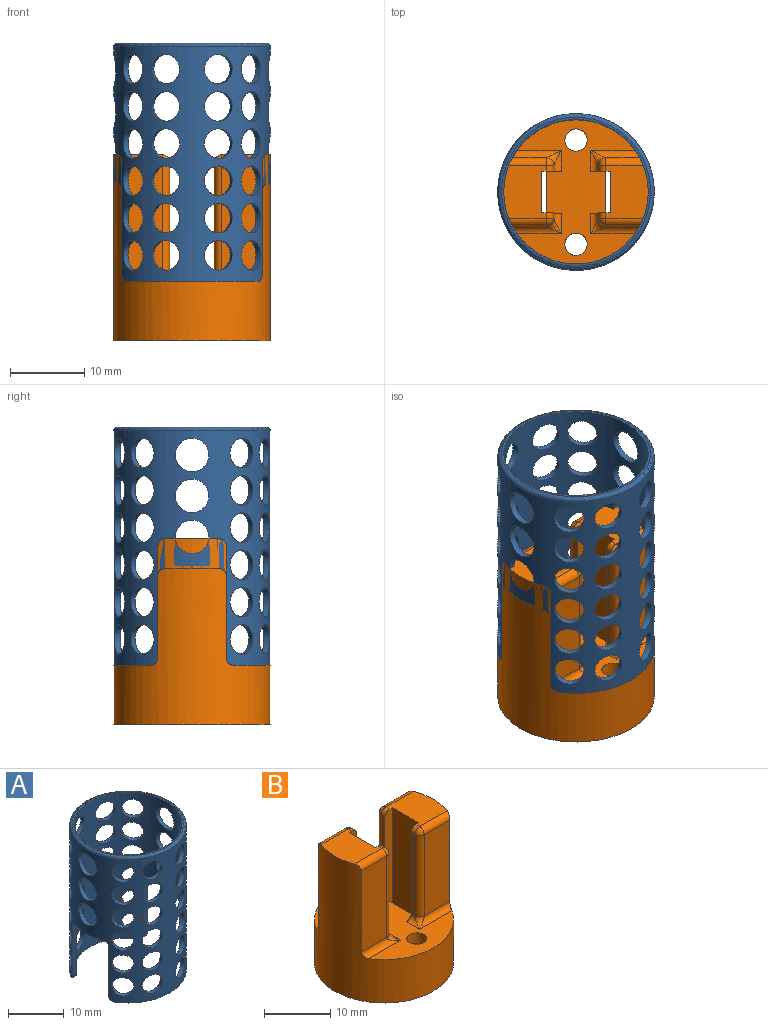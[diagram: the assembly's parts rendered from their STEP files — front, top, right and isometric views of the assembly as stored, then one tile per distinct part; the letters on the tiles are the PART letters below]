
ASSEMBLY  parts=2 mates=1
PART A: 74 faces, bbox 22.8x22.8x32 mm
  f0: cylinder r=9.7mm len=32mm, axis (0,0,-1), area 999.1mm2, adj f2,f3,f4,f5,f6,f7,f8,f9
  f1: cylinder r=10.5mm len=31.5mm, axis (0,0,-1), area 1129.1mm2, adj f2,f4,f5,f6,f7,f8,f9,f10
  f2: plane 17.76x4.9mm, normal (0,0,-1), area 15.9mm2, adj f0,f1,f61,f63
  f3: plane 20x20mm, normal (0,0,1), area 18.6mm2, adj f0,f73
  f4: plane 17.76x4.9mm, normal (0,0,-1), area 15.9mm2, adj f0,f1,f62,f66
  f5: plane 11.02x0.92mm, normal (0,1,0), area 9.8mm2, adj f0,f1,f17,f18,f65,f66
  f6: plane 7.2x1.49mm, normal (0,0,-1), area 5.9mm2, adj f0,f1,f64,f65
  f7: plane 11.02x0.92mm, normal (0,-1,0), area 9.8mm2, adj f0,f1,f15,f16,f63,f64
  f8: plane 7.2x1.49mm, normal (0,0,-1), area 5.9mm2, adj f0,f1,f59,f60
  f9: plane 11.02x0.92mm, normal (0,-1,0), area 9.8mm2, adj f0,f1,f13,f14,f59,f61
  f10: plane 11.02x0.92mm, normal (0,1,0), area 9.8mm2, adj f0,f1,f11,f12,f60,f62
  f11: cylinder r=2mm len=4mm, axis (-0.77,0.64,0), area 10.1mm2, adj f0,f1,f10
  f12: cylinder r=2mm len=4mm, axis (-0.77,0.64,0), area 10.1mm2, adj f0,f1,f10
  f13: cylinder r=2mm len=4mm, axis (-0.77,-0.64,0), area 10.1mm2, adj f0,f1,f9
  f14: cylinder r=2mm len=4mm, axis (-0.77,-0.64,0), area 10.1mm2, adj f0,f1,f9
  f15: cylinder r=2mm len=4mm, axis (0.77,-0.64,0), area 10.1mm2, adj f0,f1,f7
  f16: cylinder r=2mm len=4mm, axis (0.77,-0.64,0), area 10.1mm2, adj f0,f1,f7
  f17: cylinder r=2mm len=4mm, axis (0.77,0.64,0), area 10.1mm2, adj f0,f1,f5
  f18: cylinder r=2mm len=4mm, axis (0.77,0.64,0), area 10.1mm2, adj f0,f1,f5
  f19: cylinder r=2mm len=4.1mm, axis (-0.34,-0.94,0), area 10.2mm2, adj f0,f1
  f20: cylinder r=2mm len=4mm, axis (-0.77,-0.64,0), area 10.2mm2, adj f0,f1
  f21: cylinder r=2mm len=4.1mm, axis (0.34,-0.94,0), area 10.2mm2, adj f0,f1
  f22: cylinder r=2mm len=4mm, axis (0.77,-0.64,0), area 10.2mm2, adj f0,f1
  f23: cylinder r=2mm len=4.1mm, axis (-0.34,0.94,0), area 10.2mm2, adj f0,f1
  f24: cylinder r=2mm len=4mm, axis (-0.77,0.64,0), area 10.2mm2, adj f0,f1
  f25: cylinder r=2mm len=4.1mm, axis (0.34,0.94,0), area 10.2mm2, adj f0,f1
  f26: cylinder r=2mm len=4mm, axis (0.77,0.64,0), area 10.2mm2, adj f0,f1
  f27: cylinder r=2mm len=4.1mm, axis (-0.34,-0.94,0), area 10.2mm2, adj f0,f1
  f28: cylinder r=2mm len=4mm, axis (-0.77,-0.64,0), area 10.2mm2, adj f0,f1
  f29: cylinder r=2mm len=4.1mm, axis (0.34,-0.94,0), area 10.2mm2, adj f0,f1
  f30: cylinder r=2mm len=4mm, axis (0.77,-0.64,0), area 10.2mm2, adj f0,f1
  f31: cylinder r=2mm len=4.1mm, axis (-0.34,0.94,0), area 10.2mm2, adj f0,f1
  f32: cylinder r=2mm len=4mm, axis (-0.77,0.64,0), area 10.2mm2, adj f0,f1
  f33: cylinder r=2mm len=4.1mm, axis (0.34,0.94,0), area 10.2mm2, adj f0,f1
  f34: cylinder r=2mm len=4mm, axis (0.77,0.64,0), area 10.2mm2, adj f0,f1
  f35: cylinder r=2mm len=4.1mm, axis (-0.34,-0.94,0), area 10.2mm2, adj f0,f1
  f36: cylinder r=2mm len=4mm, axis (-0.77,-0.64,0), area 10.2mm2, adj f0,f1
  f37: cylinder r=2mm len=4.1mm, axis (0.34,-0.94,0), area 10.2mm2, adj f0,f1
  f38: cylinder r=2mm len=4mm, axis (0.77,-0.64,0), area 10.2mm2, adj f0,f1
  f39: cylinder r=2mm len=4.1mm, axis (-0.34,0.94,0), area 10.2mm2, adj f0,f1
  f40: cylinder r=2mm len=4mm, axis (-0.77,0.64,0), area 10.2mm2, adj f0,f1
  f41: cylinder r=2mm len=4.1mm, axis (0.34,0.94,0), area 10.2mm2, adj f0,f1
  f42: cylinder r=2mm len=4mm, axis (0.77,0.64,0), area 10.2mm2, adj f0,f1
  f43: cylinder r=2mm len=4.1mm, axis (-0.34,-0.94,0), area 10.2mm2, adj f0,f1
  f44: cylinder r=2mm len=4mm, axis (-0.77,-0.64,0), area 10.2mm2, adj f0,f1
  f45: cylinder r=2mm len=4.1mm, axis (0.34,-0.94,0), area 10.2mm2, adj f0,f1
  f46: cylinder r=2mm len=4mm, axis (0.77,-0.64,0), area 10.2mm2, adj f0,f1
  f47: cylinder r=2mm len=4.1mm, axis (-0.34,0.94,0), area 10.2mm2, adj f0,f1
  f48: cylinder r=2mm len=4mm, axis (-0.77,0.64,0), area 10.2mm2, adj f0,f1
  f49: cylinder r=2mm len=4.1mm, axis (0.34,0.94,0), area 10.2mm2, adj f0,f1
  f50: cylinder r=2mm len=4mm, axis (0.77,0.64,0), area 10.2mm2, adj f0,f1
  f51: cylinder r=2mm len=4.1mm, axis (-0.34,-0.94,0), area 10.2mm2, adj f0,f1
  f52: cylinder r=2mm len=4.1mm, axis (0.34,-0.94,0), area 10.2mm2, adj f0,f1
  f53: cylinder r=2mm len=4.1mm, axis (-0.34,0.94,0), area 10.2mm2, adj f0,f1
  f54: cylinder r=2mm len=4.1mm, axis (0.34,0.94,0), area 10.2mm2, adj f0,f1
  f55: cylinder r=2mm len=4.1mm, axis (-0.34,-0.94,0), area 10.2mm2, adj f0,f1
  f56: cylinder r=2mm len=4.1mm, axis (0.34,-0.94,0), area 10.2mm2, adj f0,f1
  f57: cylinder r=2mm len=4.1mm, axis (-0.34,0.94,0), area 10.2mm2, adj f0,f1
  f58: cylinder r=2mm len=4.1mm, axis (0.34,0.94,0), area 10.2mm2, adj f0,f1
  f59: cylinder r=1mm len=1.32mm, axis (-1,0,0), area 1.4mm2, adj f0,f1,f8,f9
  f60: cylinder r=1mm len=1.32mm, axis (-1,0,0), area 1.4mm2, adj f0,f1,f8,f10
  f61: cylinder r=1mm len=1.52mm, axis (-1,0,0), area 1.4mm2, adj f0,f1,f2,f9
  f62: cylinder r=1mm len=1.52mm, axis (-1,0,0), area 1.4mm2, adj f0,f1,f4,f10
  f63: cylinder r=1mm len=1.52mm, axis (-1,0,0), area 1.4mm2, adj f0,f1,f2,f7
  f64: cylinder r=1mm len=1.32mm, axis (-1,0,0), area 1.4mm2, adj f0,f1,f6,f7
  f65: cylinder r=1mm len=1.32mm, axis (-1,0,0), area 1.4mm2, adj f0,f1,f5,f6
  f66: cylinder r=1mm len=1.52mm, axis (-1,0,0), area 1.4mm2, adj f0,f1,f4,f5
  f67: cylinder r=2.25mm len=4.5mm, axis (1,0,0), area 11.5mm2, adj f0,f1
  f68: cylinder r=2.25mm len=4.5mm, axis (1,0,0), area 11.5mm2, adj f0,f1
  f69: cylinder r=2.25mm len=4.5mm, axis (1,0,0), area 11.5mm2, adj f0,f1
  f70: cylinder r=2.25mm len=4.5mm, axis (1,0,0), area 11.5mm2, adj f0,f1
  f71: cylinder r=2.25mm len=4.5mm, axis (1,0,0), area 11.5mm2, adj f0,f1
  f72: cylinder r=2.25mm len=4.5mm, axis (1,0,0), area 11.5mm2, adj f0,f1
  f73: torus R=10mm, axis (0,0,1), area 50.9mm2, adj f1,f3
PART B: 116 faces, bbox 21.3x21.3x25.3 mm
  f0: plane 7.2x6.5mm, normal (0,0,1), area 41.9mm2, adj f2,f40,f41,f44,f56,f57,f58,f59
  f1: plane 12.4x9.4mm, normal (0,0,-1), area 26.6mm2, adj f21,f23,f24,f27,f29,f30,f48,f50
  f2: cylinder r=10.5mm len=25mm, axis (0,0,1), area 851.6mm2, adj f0,f3,f6,f31,f32,f37,f38,f43
  f3: plane 7.2x6.5mm, normal (0,0,1), area 41.9mm2, adj f2,f34,f35,f46,f60,f61,f62,f63
  f4: cylinder r=1.5mm len=3.34mm, axis (0,0,-1), area 23.1mm2, adj f18,f31,f100
  f5: cylinder r=1.5mm len=3.34mm, axis (0,0,-1), area 23.1mm2, adj f12,f31,f101
  f6: plane 21x21mm, normal (0,0,-1), area 119.9mm2, adj f2,f7,f8,f9,f10,f11,f13,f14
  f7: plane 4.5x1.2mm, normal (-1,0,0), area 5.4mm2, adj f6,f8,f98,f105
  f8: plane 4.5x4.13mm, normal (0,1,0), area 18.6mm2, adj f6,f7,f99,f104
  f9: plane 4.5x1.55mm, normal (0.91,0.41,0), area 7.6mm2, adj f6,f10,f99,f102
  f10: plane 6.26x5.16mm, normal (0,1,0), area 18.8mm2, adj f6,f9,f11,f101,f102
  f11: cylinder r=9mm len=11.01mm, axis (0,0,-1), area 37.1mm2, adj f6,f10,f101,f108
  f12: plane 3.92x1.71mm, normal (0,0,-1), area 4.8mm2, adj f5,f101,f102,f103,f104,f106
  f13: cylinder r=9mm len=11.01mm, axis (0,0,-1), area 37.1mm2, adj f6,f17,f100,f115
  f14: plane 4.5x1.2mm, normal (1,0,0), area 5.4mm2, adj f6,f15,f95,f112
  f15: plane 4.5x4.13mm, normal (0,-1,0), area 18.6mm2, adj f6,f14,f94,f111
  f16: plane 4.5x1.55mm, normal (-0.91,-0.41,0), area 7.6mm2, adj f6,f17,f94,f109
  f17: plane 6.26x5.16mm, normal (0,-1,0), area 18.8mm2, adj f6,f13,f16,f100,f109
  f18: plane 3.92x1.71mm, normal (0,0,-1), area 4.8mm2, adj f4,f100,f109,f110,f111,f113
  f19: cylinder r=9.7mm len=8.05mm, axis (0,0,-1), area 20.8mm2, adj f6,f30,f85,f89
  f20: plane 4.4x2.16mm, normal (0,1,0), area 8.7mm2, adj f6,f86,f87,f88,f89
  f21: plane 6.33x3.65mm, normal (0.91,0.41,0), area 12.1mm2, adj f1,f6,f22,f49,f51,f86,f87,f97
  f22: plane 6.4x4.4mm, normal (0,1,0), area 28.2mm2, adj f6,f21,f23,f97
  f23: plane 6x4.6mm, normal (-1,0,0), area 18.5mm2, adj f1,f6,f22,f24,f97
  f24: plane 6x5.29mm, normal (0,1,0), area 28.6mm2, adj f1,f6,f23,f25,f84
  f25: cylinder r=9.7mm len=8.05mm, axis (0,0,-1), area 20.8mm2, adj f6,f24,f84,f93
  f26: plane 4.4x2.16mm, normal (0,-1,0), area 8.7mm2, adj f6,f90,f91,f92,f93
  f27: plane 6.33x3.65mm, normal (-0.91,-0.41,0), area 12.1mm2, adj f1,f6,f28,f53,f55,f90,f91,f96
  f28: plane 6.4x4.4mm, normal (0,-1,0), area 28.2mm2, adj f6,f27,f29,f96
  f29: plane 6x4.6mm, normal (1,0,0), area 18.5mm2, adj f1,f6,f28,f30,f96
  f30: plane 6x5.29mm, normal (0,-1,0), area 28.6mm2, adj f1,f6,f19,f29,f85
  f31: plane 21x17.76mm, normal (0,0,1), area 175.9mm2, adj f2,f4,f5,f34,f35,f40,f41,f45
  f32: plane 15x5.44mm, normal (0,-1,0), area 81.6mm2, adj f2,f62,f70,f73
  f33: plane 15x0.8mm, normal (-1,0,0), area 12mm2, adj f34,f63,f71,f73
  f34: plane 18.75x2.6mm, normal (0,1,0), area 28.2mm2, adj f3,f31,f33,f46,f47,f49,f63,f71
  f35: plane 18.75x2.6mm, normal (0,-1,0), area 28.2mm2, adj f3,f31,f36,f46,f47,f50,f60,f68
  f36: plane 15x0.8mm, normal (-1,0,0), area 12mm2, adj f35,f60,f68,f76
  f37: plane 15x5.44mm, normal (0,1,0), area 81.6mm2, adj f2,f61,f69,f76
  f38: plane 15x5.44mm, normal (0,1,0), area 81.6mm2, adj f2,f58,f66,f79
  f39: plane 15x0.8mm, normal (1,0,0), area 12mm2, adj f40,f59,f67,f79
  f40: plane 18.75x2.6mm, normal (0,-1,0), area 28.2mm2, adj f0,f31,f39,f44,f45,f53,f59,f67
  f41: plane 18.75x2.6mm, normal (0,1,0), area 28.2mm2, adj f0,f31,f42,f44,f45,f54,f56,f64
  f42: plane 15x0.8mm, normal (1,0,0), area 12mm2, adj f41,f56,f64,f82
  f43: plane 15x5.44mm, normal (0,-1,0), area 81.6mm2, adj f2,f57,f65,f82
  f44: plane 18.75x5.6mm, normal (1,0,0), area 105mm2, adj f0,f40,f41,f52
  f45: plane 5.6x1.75mm, normal (-1,0,0), area 9.8mm2, adj f31,f40,f41,f55
  f46: plane 18.75x5.6mm, normal (-1,0,0), area 105mm2, adj f3,f34,f35,f48
  f47: plane 5.6x1.75mm, normal (1,0,0), area 9.8mm2, adj f31,f34,f35,f51
  f48: plane 6.14x0.29mm, normal (-0.71,0,-0.71), area 2.1mm2, adj f1,f46,f49,f50,f87
  f49: plane 1.09x0.27mm, normal (0,0.71,-0.71), area 0.3mm2, adj f21,f34,f48,f51,f87
  f50: plane 1.1x0.25mm, normal (0,-0.71,-0.71), area 0.3mm2, adj f1,f35,f48,f51
  f51: plane 6.07x0.25mm, normal (0.71,0,-0.71), area 2.1mm2, adj f1,f21,f47,f49,f50
  f52: plane 6.14x0.29mm, normal (0.71,0,-0.71), area 2.1mm2, adj f1,f44,f53,f54,f91
  f53: plane 1.09x0.27mm, normal (0,-0.71,-0.71), area 0.3mm2, adj f27,f40,f52,f55,f91
  f54: plane 1.1x0.25mm, normal (0,0.71,-0.71), area 0.3mm2, adj f1,f41,f52,f55
  f55: plane 6.07x0.25mm, normal (-0.71,0,-0.71), area 2.1mm2, adj f1,f27,f45,f53,f54
  f56: cylinder r=1mm len=1mm, axis (0,1,0), area 1.3mm2, adj f0,f41,f42,f81
  f57: cylinder r=1mm len=5.86mm, axis (1,0,0), area 8.9mm2, adj f0,f2,f43,f81
  f58: cylinder r=1mm len=5.86mm, axis (-1,0,0), area 8.9mm2, adj f0,f2,f38,f78
  f59: cylinder r=1mm len=1mm, axis (0,1,0), area 1.3mm2, adj f0,f39,f40,f78
  f60: cylinder r=1mm len=1mm, axis (0,-1,0), area 1.3mm2, adj f3,f35,f36,f75
  f61: cylinder r=1mm len=5.86mm, axis (-1,0,0), area 8.9mm2, adj f2,f3,f37,f75
  f62: cylinder r=1mm len=5.86mm, axis (1,0,0), area 8.9mm2, adj f2,f3,f32,f72
  f63: cylinder r=1mm len=1mm, axis (0,-1,0), area 1.3mm2, adj f3,f33,f34,f72
  f64: cylinder r=1mm len=2.8mm, axis (0,-1,0), area 2.4mm2, adj f31,f41,f42,f83
  f65: cylinder r=1mm len=7.44mm, axis (-1,0,0), area 9.2mm2, adj f2,f31,f43,f83
  f66: cylinder r=1mm len=7.44mm, axis (1,0,0), area 9.2mm2, adj f2,f31,f38,f80
  f67: cylinder r=1mm len=2.8mm, axis (0,-1,0), area 2.4mm2, adj f31,f39,f40,f80
  f68: cylinder r=1mm len=2.8mm, axis (0,1,0), area 2.4mm2, adj f31,f35,f36,f77
  f69: cylinder r=1mm len=7.44mm, axis (1,0,0), area 9.2mm2, adj f2,f31,f37,f77
  f70: cylinder r=1mm len=7.44mm, axis (-1,0,0), area 9.2mm2, adj f2,f31,f32,f74
  f71: cylinder r=1mm len=2.8mm, axis (0,1,0), area 2.4mm2, adj f31,f33,f34,f74
  f72: sphere r=1mm, area 1.6mm2, adj f62,f63,f73
  f73: cylinder r=1mm len=15mm, axis (0,0,1), area 23.6mm2, adj f32,f33,f72,f74
  f74: bspline ~2x2mm, area 1.9mm2, adj f70,f71,f73
  f75: sphere r=1mm, area 1.6mm2, adj f60,f61,f76
  f76: cylinder r=1mm len=15mm, axis (0,0,1), area 23.6mm2, adj f36,f37,f75,f77
  f77: bspline ~2x2mm, area 1.9mm2, adj f68,f69,f76
  f78: sphere r=1mm, area 1.6mm2, adj f58,f59,f79
  f79: cylinder r=1mm len=15mm, axis (0,0,1), area 23.6mm2, adj f38,f39,f78,f80
  f80: bspline ~2x2mm, area 1.9mm2, adj f66,f67,f79
  f81: sphere r=1mm, area 1.6mm2, adj f56,f57,f82
  f82: cylinder r=1mm len=15mm, axis (0,0,1), area 23.6mm2, adj f42,f43,f81,f83
  f83: bspline ~2x2mm, area 1.9mm2, adj f64,f65,f82
  f84: torus R=6.2mm, axis (0,0,-1), area 45.4mm2, adj f1,f24,f25,f92
  f85: torus R=6.2mm, axis (0,0,-1), area 45.4mm2, adj f1,f19,f30,f88
  f86: cylinder r=1.6mm len=5.86mm, axis (0,0,1), area 9.5mm2, adj f6,f20,f21,f87
  f87: cylinder r=1.6mm len=1.72mm, axis (1,0,0), area 2.5mm2, adj f1,f20,f21,f48,f49,f86,f88
  f88: bspline ~4.19x3.94mm, area 9.8mm2, adj f20,f85,f87,f89
  f89: cylinder r=1.6mm len=2.5mm, axis (0,0,-1), area 4.9mm2, adj f6,f19,f20,f88
  f90: cylinder r=1.6mm len=5.86mm, axis (0,0,1), area 9.5mm2, adj f6,f26,f27,f91
  f91: cylinder r=1.6mm len=1.72mm, axis (-1,0,0), area 2.5mm2, adj f1,f26,f27,f52,f53,f90,f92
  f92: bspline ~4.19x3.94mm, area 9.8mm2, adj f26,f84,f91,f93
  f93: cylinder r=1.6mm len=2.5mm, axis (0,0,-1), area 4.9mm2, adj f6,f25,f26,f92
  f94: cylinder r=1.6mm len=4.5mm, axis (0,0,1), area 8.3mm2, adj f6,f15,f16,f110
  f95: cylinder r=1.6mm len=4.5mm, axis (0,0,-1), area 8.7mm2, adj f6,f14,f113,f114,f115
  f96: cylinder r=1.6mm len=6.4mm, axis (1,0,0), area 15.2mm2, adj f1,f27,f28,f29
  f97: cylinder r=1.6mm len=6.4mm, axis (-1,0,0), area 15.2mm2, adj f1,f21,f22,f23
  f98: cylinder r=1.6mm len=4.5mm, axis (0,0,-1), area 8.7mm2, adj f6,f7,f106,f107,f108
  f99: cylinder r=1.6mm len=4.5mm, axis (0,0,1), area 8.3mm2, adj f6,f8,f9,f103
  f100: torus R=6mm, axis (0,0,-1), area 37.8mm2, adj f4,f13,f17,f18,f109,f114
  f101: torus R=6mm, axis (0,0,-1), area 37.8mm2, adj f5,f10,f11,f12,f102,f107
  f102: cylinder r=1.5mm len=2.16mm, axis (-0.41,0.91,0), area 3.3mm2, adj f9,f10,f12,f101,f103
  f103: torus R=0.1mm, axis (0,0,-1), area 2.9mm2, adj f12,f99,f102,f104
  f104: cylinder r=1.5mm len=4.13mm, axis (-1,0,0), area 8.4mm2, adj f8,f12,f103,f105,f106
  f105: cylinder r=1.5mm len=1.47mm, axis (0,1,0), area 1.6mm2, adj f7,f104,f106
  f106: torus R=3.1mm, axis (0,0,-1), area 3.3mm2, adj f12,f98,f104,f105,f107
  f107: bspline ~5.77x4.41mm, area 12.1mm2, adj f98,f101,f106,f108
  f108: cylinder r=1.5mm len=3mm, axis (0,0,-1), area 10.9mm2, adj f6,f11,f98,f107
  f109: cylinder r=1.5mm len=2.16mm, axis (0.41,-0.91,0), area 3.3mm2, adj f16,f17,f18,f100,f110
  f110: torus R=0.1mm, axis (0,0,-1), area 2.9mm2, adj f18,f94,f109,f111
  f111: cylinder r=1.5mm len=4.13mm, axis (1,0,0), area 8.4mm2, adj f15,f18,f110,f112,f113
  f112: cylinder r=1.5mm len=1.47mm, axis (0,-1,0), area 1.6mm2, adj f14,f111,f113
  f113: torus R=3.1mm, axis (0,0,-1), area 3.3mm2, adj f18,f95,f111,f112,f114
  f114: bspline ~5.77x4.41mm, area 12.1mm2, adj f95,f100,f113,f115
  f115: cylinder r=1.5mm len=3mm, axis (0,0,-1), area 10.9mm2, adj f6,f13,f95,f114
PLACE A t=(0,0,-4)mm
PLACE B t=(0,0,13)mm
MATE fastened A.f0 <-> B.f2  axis (0,0,-1) through (0,0,-4)mm
